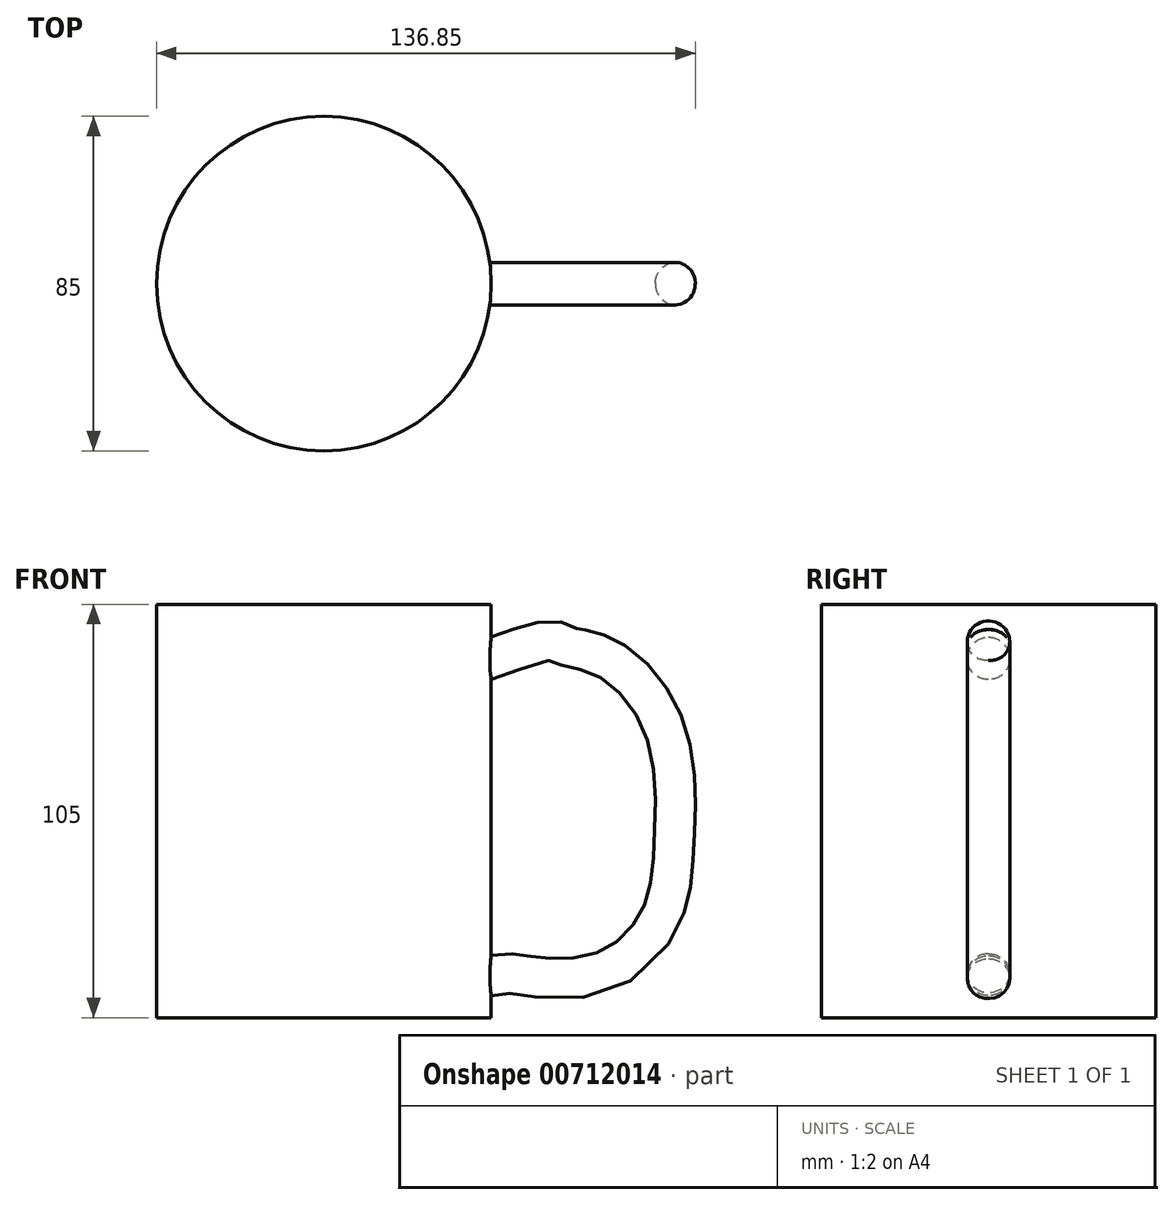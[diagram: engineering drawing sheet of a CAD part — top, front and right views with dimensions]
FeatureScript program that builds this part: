
annotation { "Feature Type Name" : "Feature", "Feature Type Description" : "" }
export const myFeature = defineFeature(function(context is Context, id is Id, definition is map)
    precondition{}
    {
        {
            var Q0;
            Q0=qCreatedBy(makeId("Top.planeOp"),FACE);
            var sketch = newSketch(context, id + "F0", { "sketchPlane" : qUnion([Q0])});
            skCircle(sketch, "E0", {"center": v(0, 0) * mm, "radius": 42.5 * mm});
            skSolve(sketch);
        }
        {
            var Q0;
            Q0 = qSketchRegion(id + "F0", true);
            extrude(context, id + "F1", {"entities" : qUnion([Q0]), "depth" : 105 * mm, "offsetDistance" : 25.4 * mm});
        }
        {
            var Q0;
            Q0=qCreatedBy(makeId("Front.planeOp"),FACE);
            var sketch = newSketch(context, id + "F2", { "sketchPlane" : qUnion([Q0])});
            skFitSpline(sketch, "E1", {"points": [v(39.5, 87.71) * mm, v(57.2, 93.22) * mm, v(60.34, 92.43) * mm, v(71.35, 88.9) * mm, v(84.71, 71.6) * mm, v(86.68, 45.65) * mm, v(83.53, 26.78) * mm, v(70.95, 14.2) * mm, v(54.44, 12.63) * mm, v(45.4, 13.42) * mm, v(37.54, 13.02) * mm, v(36.75, 17.35) * mm], "startDerivative": vector(201.86, 75.5) * mm, "endDerivative": vector(7.55, 103.44) * mm});
            skSolve(sketch);
        }
        {
            var Q0;
            Q0=qCreatedBy(makeId("Right.planeOp"),FACE);
            cPlane(context, id + "F3", {"entities" : qUnion([Q0]), "cplaneType" : CPlaneType.OFFSET, "offset" : 40 * mm, "width" : 152.4 * mm, "height" : 152.4 * mm});
        }
        {
            var Q0;
            Q0=qCreatedBy(id+"F3.planeOp",FACE);
            var sketch = newSketch(context, id + "F4", { "sketchPlane" : qUnion([Q0])});
            skCircle(sketch, "E2", {"center": v(0, 90.38) * mm, "radius": 5.4 * mm});
            skSolve(sketch);
        }
        {
            var Q0;
            Q0 = qSketchRegion(id + "F4", true);
            var Q1;
            Q1=sQuery(id+"F2.wireOp",EDGE,"E1");
            sweep(context, id + "F5", {"operationType" : NewBodyOperationType.ADD, "profiles" : qUnion([Q0]), "path" : qUnion([Q1])});
        }
    });
